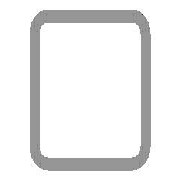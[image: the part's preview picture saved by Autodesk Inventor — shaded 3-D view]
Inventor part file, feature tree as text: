
AUTODESK INVENTOR PART (.ipt)
format: ipt  version: 2025.3 (Build 293356030, 356C)  size: 147,456 bytes
history: native  units: mm (DEFAULTED — no unit token found)
features: other x4, sketch x1, plane x1
ambient origin geometry x8: Origin, YZ Plane, XZ Plane, XY Plane, X Axis, Y Axis, Z Axis, Center Point
bodies: Solid1 (feature_tree), Body (feature_tree)
feature tree (6):
  parser-record x1  (decoder bookkeeping rows leaked as tree rows — omitted from the tree; the rows remain in map.json)
  other  "Driven Length"
  other  "Start Plane"
  other  "End Plane"
  sketch  "Sketch3"  dims[d3=260.0mm d4=0.0mm d7=4.0mm d9=40.0mm d11=40.0mm d12=2.0mm d13=40.0mm d14=300.0mm d15=20.0mm d16=20.0mm d17=90.0deg d18=260.0mm]
  plane  "Work Plane3"
